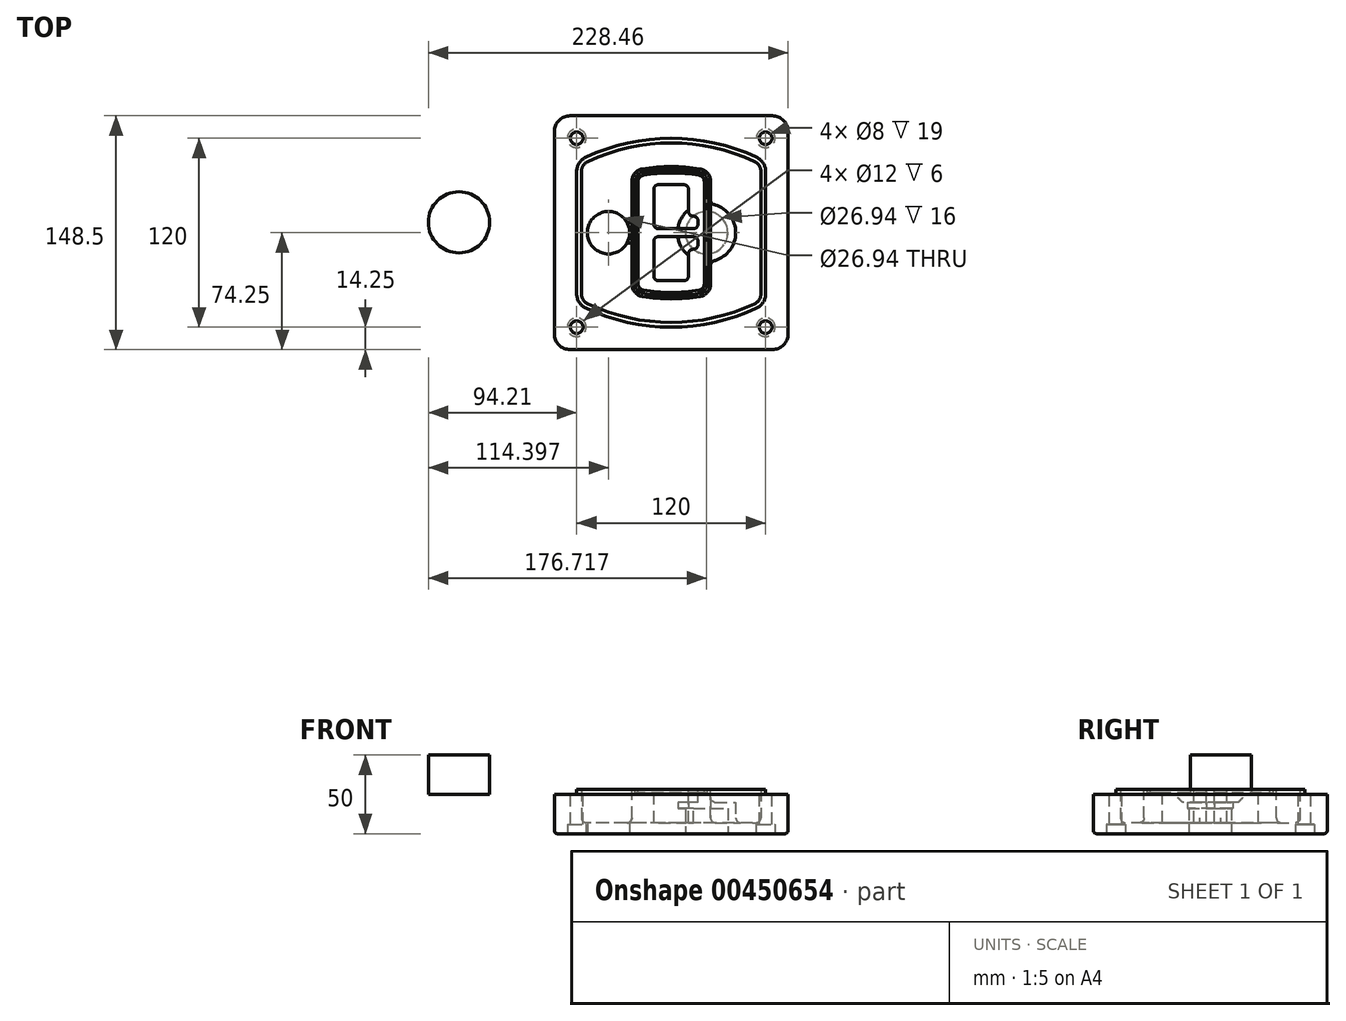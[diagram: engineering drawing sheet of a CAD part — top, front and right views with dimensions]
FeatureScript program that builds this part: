
annotation { "Feature Type Name" : "Feature", "Feature Type Description" : "" }
export const myFeature = defineFeature(function(context is Context, id is Id, definition is map)
    precondition{}
    {
        {
            var Q0;
            Q0=qCreatedBy(makeId("Top.planeOp"),FACE);
            var sketch = newSketch(context, id + "F0", { "sketchPlane" : qUnion([Q0])});
            skPoint(sketch, "E0.rect.middle", {"position": v(0, 0) * mm});
            skLineSegment(sketch, "E1.bottom", {"start": v(-64.25, -74.25) * mm, "end": v(64.25, -74.25) * mm});
            skLineSegment(sketch, "E1.top", {"start": v(-64.25, 74.25) * mm, "end": v(64.25, 74.25) * mm});
            skLineSegment(sketch, "E1.left", {"start": v(-74.25, -64.25) * mm, "end": v(-74.25, 64.25) * mm});
            skLineSegment(sketch, "E1.right", {"start": v(74.25, -64.25) * mm, "end": v(74.25, 64.25) * mm});
            skLineSegment(sketch, "E2", {"start": v(-74.25, 74.25) * mm, "end": v(74.25, -74.25) * mm, "construction": true});
            skLineSegment(sketch, "E3", {"start": v(74.25, 74.25) * mm, "end": v(-74.25, -74.25) * mm, "construction": true});
            skCircle(sketch, "E4", {"center": v(-60, 60) * mm, "radius": 4 * mm});
            skCircle(sketch, "E5", {"center": v(60, 60) * mm, "radius": 4 * mm});
            skCircle(sketch, "E6", {"center": v(60, -60) * mm, "radius": 4 * mm});
            skCircle(sketch, "E7", {"center": v(-60, -60) * mm, "radius": 4 * mm});
            skLineSegment(sketch, "E8", {"start": v(-60, 60) * mm, "end": v(60, 60) * mm, "construction": true});
            skLineSegment(sketch, "E9", {"start": v(60, 60) * mm, "end": v(60, -60) * mm, "construction": true});
            skLineSegment(sketch, "E10", {"start": v(60, -60) * mm, "end": v(-60, -60) * mm, "construction": true});
            skLineSegment(sketch, "E11", {"start": v(-60, -60) * mm, "end": v(-60, 60) * mm, "construction": true});
            skLineSegment(sketch, "E12", {"start": v(-60, 38.83) * mm, "end": v(-60, -38.83) * mm});
            skLineSegment(sketch, "E13", {"start": v(60, 38.83) * mm, "end": v(60, -38.83) * mm});
            skArc(sketch, "E14", {"start": v(54.26, 47.88) * mm, "mid": v(0, 60) * mm, "end": v(-54.26, 47.88) * mm});
            skArc(sketch, "E15", {"start": v(-54.26, -47.88) * mm, "mid": v(0, -60) * mm, "end": v(54.26, -47.88) * mm});
            skLineSegment(sketch, "E16", {"start": v(-60, 0) * mm, "end": v(60, 0) * mm, "construction": true});
            skPoint(sketch, "E17.visualSharp", {"position": v(-60, -45) * mm});
            skArc(sketch, "E17.filletArc", {"start": v(-60, -38.83) * mm, "mid": v(-58.44, -44.2) * mm, "end": v(-54.26, -47.88) * mm});
            skPoint(sketch, "E18.visualSharp", {"position": v(-60, 45) * mm});
            skArc(sketch, "E18.filletArc", {"start": v(-54.26, 47.88) * mm, "mid": v(-58.44, 44.2) * mm, "end": v(-60, 38.83) * mm});
            skPoint(sketch, "E19.visualSharp", {"position": v(60, 45) * mm});
            skArc(sketch, "E19.filletArc", {"start": v(60, 38.83) * mm, "mid": v(58.44, 44.2) * mm, "end": v(54.26, 47.88) * mm});
            skPoint(sketch, "E20.visualSharp", {"position": v(60, -45) * mm});
            skArc(sketch, "E20.filletArc", {"start": v(54.26, -47.88) * mm, "mid": v(58.44, -44.2) * mm, "end": v(60, -38.83) * mm});
            skPoint(sketch, "E21.visualSharp", {"position": v(-74.25, 74.25) * mm});
            skArc(sketch, "E21.filletArc", {"start": v(-64.25, 74.25) * mm, "mid": v(-71.32, 71.32) * mm, "end": v(-74.25, 64.25) * mm});
            skPoint(sketch, "E22.visualSharp", {"position": v(74.25, 74.25) * mm});
            skArc(sketch, "E22.filletArc", {"start": v(74.25, 64.25) * mm, "mid": v(71.32, 71.32) * mm, "end": v(64.25, 74.25) * mm});
            skPoint(sketch, "E23.visualSharp", {"position": v(74.25, -74.25) * mm});
            skArc(sketch, "E23.filletArc", {"start": v(64.25, -74.25) * mm, "mid": v(71.32, -71.32) * mm, "end": v(74.25, -64.25) * mm});
            skPoint(sketch, "E24.visualSharp", {"position": v(-74.25, -74.25) * mm});
            skArc(sketch, "E24.filletArc", {"start": v(-74.25, -64.25) * mm, "mid": v(-71.32, -71.32) * mm, "end": v(-64.25, -74.25) * mm});
            skArc(sketch, "E25.0", {"start": v(57, 38.83) * mm, "mid": v(55.9, 42.58) * mm, "end": v(52.98, 45.17) * mm});
            skLineSegment(sketch, "E25.1", {"start": v(57, 38.83) * mm, "end": v(57, -38.83) * mm});
            skArc(sketch, "E25.2", {"start": v(52.98, -45.17) * mm, "mid": v(55.9, -42.58) * mm, "end": v(57, -38.83) * mm});
            skArc(sketch, "E25.3", {"start": v(-52.98, -45.17) * mm, "mid": v(0, -57) * mm, "end": v(52.98, -45.17) * mm});
            skArc(sketch, "E25.4", {"start": v(-57, -38.83) * mm, "mid": v(-55.9, -42.58) * mm, "end": v(-52.98, -45.17) * mm});
            skArc(sketch, "E25.5", {"start": v(52.98, 45.17) * mm, "mid": v(0, 57) * mm, "end": v(-52.98, 45.17) * mm});
            skLineSegment(sketch, "E25.6", {"start": v(-57, 38.83) * mm, "end": v(-57, -38.83) * mm});
            skArc(sketch, "E25.7", {"start": v(-52.98, 45.17) * mm, "mid": v(-55.9, 42.58) * mm, "end": v(-57, 38.83) * mm});
            skArc(sketch, "E26.0", {"start": v(-55.96, 51.5) * mm, "mid": v(-61.82, 46.33) * mm, "end": v(-64, 38.83) * mm});
            skArc(sketch, "E26.1", {"start": v(55.96, 51.5) * mm, "mid": v(0, 64) * mm, "end": v(-55.96, 51.5) * mm});
            skArc(sketch, "E26.2", {"start": v(64, 38.83) * mm, "mid": v(61.82, 46.33) * mm, "end": v(55.96, 51.5) * mm});
            skLineSegment(sketch, "E26.3", {"start": v(64, 38.83) * mm, "end": v(64, -38.83) * mm});
            skArc(sketch, "E26.4", {"start": v(55.96, -51.5) * mm, "mid": v(61.82, -46.33) * mm, "end": v(64, -38.83) * mm});
            skLineSegment(sketch, "E26.5", {"start": v(-64, 38.83) * mm, "end": v(-64, -38.83) * mm});
            skArc(sketch, "E26.6", {"start": v(-55.96, -51.5) * mm, "mid": v(0, -64) * mm, "end": v(55.96, -51.5) * mm});
            skArc(sketch, "E26.7", {"start": v(-64, -38.83) * mm, "mid": v(-61.82, -46.33) * mm, "end": v(-55.96, -51.5) * mm});
            skSolve(sketch);
        }
        {
            var Q0;
            Q0=makeQuery(id+"F0.imprint","IMPRINT",FACE,{"disambiguationData":[TD([[makeQuery(id+"F0.imprint","IMPRINT",EDGE,{"derivedFrom":sQuery(id+"F0.wireOp",EDGE,"E1.bottom")}),1.0]])]});
            var Q1;
            Q1=makeQuery(id+"F0.imprint","IMPRINT",FACE,{"disambiguationData":[TD([[makeQuery(id+"F0.imprint","IMPRINT",EDGE,{"derivedFrom":sQuery(id+"F0.wireOp",EDGE,"E12")}),1.0]])]});
            var Q2;
            Q2=makeQuery(id+"F0.imprint","IMPRINT",FACE,{"disambiguationData":[TD([[makeQuery(id+"F0.imprint","IMPRINT",EDGE,{"derivedFrom":sQuery(id+"F0.wireOp",EDGE,"E25.0")}),1.0]])]});
            var Q3;
            Q3=makeQuery(id+"F0.imprint","IMPRINT",FACE,{"disambiguationData":[TD([[makeQuery(id+"F0.imprint","IMPRINT",EDGE,{"derivedFrom":sQuery(id+"F0.wireOp",EDGE,"E12")}),-1.0]])]});
            extrude(context, id + "F1", {"entities" : qUnion([Q0, Q1, Q2, Q3]), "oppositeDirection" : true, "depth" : 25 * mm});
        }
        {
            var Q0;
            Q0=makeQuery(id+"F0.imprint","IMPRINT",FACE,{"disambiguationData":[TD([[makeQuery(id+"F0.imprint","IMPRINT",EDGE,{"derivedFrom":sQuery(id+"F0.wireOp",EDGE,"E12")}),1.0]])]});
            extrude(context, id + "F2", {"entities" : qUnion([Q0]), "operationType" : NewBodyOperationType.ADD, "depth" : 3 * mm});
        }
        {
            var Q0;
            Q0=makeQuery(id+"F0.imprint","IMPRINT",FACE,{"disambiguationData":[TD([[makeQuery(id+"F0.imprint","IMPRINT",EDGE,{"derivedFrom":sQuery(id+"F0.wireOp",EDGE,"E25.0")}),1.0]])]});
            extrude(context, id + "F3", {"entities" : qUnion([Q0]), "operationType" : NewBodyOperationType.REMOVE, "oppositeDirection" : true, "depth" : 18 * mm});
        }
        {
            var Q0;
            Q0=makeQuery(id+"F2.opExtrude","CAP_FACE",FACE,{"disambiguationData":[OSD([sQuery(id+"F0.wireOp",EDGE,"E12"),sQuery(id+"F0.wireOp",EDGE,"E13"),sQuery(id+"F0.wireOp",EDGE,"E14"),sQuery(id+"F0.wireOp",EDGE,"E15"),sQuery(id+"F0.wireOp",EDGE,"E17.filletArc"),sQuery(id+"F0.wireOp",EDGE,"E18.filletArc"),sQuery(id+"F0.wireOp",EDGE,"E19.filletArc"),sQuery(id+"F0.wireOp",EDGE,"E20.filletArc"),sQuery(id+"F0.wireOp",EDGE,"E25.0"),sQuery(id+"F0.wireOp",EDGE,"E25.1"),sQuery(id+"F0.wireOp",EDGE,"E25.2"),sQuery(id+"F0.wireOp",EDGE,"E25.3"),sQuery(id+"F0.wireOp",EDGE,"E25.4"),sQuery(id+"F0.wireOp",EDGE,"E25.5"),sQuery(id+"F0.wireOp",EDGE,"E25.6"),sQuery(id+"F0.wireOp",EDGE,"E25.7")])],"isStart":false});
            var sketch = newSketch(context, id + "F4", { "sketchPlane" : qUnion([Q0])});
            skArc(sketch, "E27.0", {"start": v(-18.34, -40.45) * mm, "mid": v(0, -42) * mm, "end": v(18.34, -40.45) * mm});
            skArc(sketch, "E28.0", {"start": v(18.34, 40.45) * mm, "mid": v(0, 42) * mm, "end": v(-18.34, 40.45) * mm});
            skLineSegment(sketch, "E29", {"start": v(-25, 32.57) * mm, "end": v(-25, -32.57) * mm});
            skLineSegment(sketch, "E30", {"start": v(25, 32.57) * mm, "end": v(25, -32.57) * mm});
            skLineSegment(sketch, "E31", {"start": v(-25, 39.1) * mm, "end": v(25, 39.1) * mm, "construction": true});
            skLineSegment(sketch, "E32", {"start": v(-25, -39.1) * mm, "end": v(25, -39.1) * mm, "construction": true});
            skPoint(sketch, "E33.visualSharp", {"position": v(-25, 39.1) * mm});
            skArc(sketch, "E33.filletArc", {"start": v(-18.34, 40.45) * mm, "mid": v(-23.11, 37.73) * mm, "end": v(-25, 32.57) * mm});
            skPoint(sketch, "E34.visualSharp", {"position": v(25, 39.1) * mm});
            skArc(sketch, "E34.filletArc", {"start": v(25, 32.57) * mm, "mid": v(23.11, 37.73) * mm, "end": v(18.34, 40.45) * mm});
            skPoint(sketch, "E35.visualSharp", {"position": v(25, -39.1) * mm});
            skArc(sketch, "E35.filletArc", {"start": v(18.34, -40.45) * mm, "mid": v(23.11, -37.73) * mm, "end": v(25, -32.57) * mm});
            skPoint(sketch, "E36.visualSharp", {"position": v(-25, -39.1) * mm});
            skArc(sketch, "E36.filletArc", {"start": v(-25, -32.57) * mm, "mid": v(-23.11, -37.73) * mm, "end": v(-18.34, -40.45) * mm});
            skArc(sketch, "E37.0", {"start": v(52.98, 45.17) * mm, "mid": v(0, 57) * mm, "end": v(-52.98, 45.17) * mm});
            skArc(sketch, "E37.1", {"start": v(-52.98, 45.17) * mm, "mid": v(-55.9, 42.58) * mm, "end": v(-57, 38.83) * mm});
            skLineSegment(sketch, "E37.2", {"start": v(-57, 38.83) * mm, "end": v(-57, -38.83) * mm});
            skArc(sketch, "E37.3", {"start": v(-57, -38.83) * mm, "mid": v(-55.9, -42.58) * mm, "end": v(-52.98, -45.17) * mm});
            skArc(sketch, "E37.4", {"start": v(-52.98, -45.17) * mm, "mid": v(0, -57) * mm, "end": v(52.98, -45.17) * mm});
            skArc(sketch, "E37.5", {"start": v(52.98, -45.17) * mm, "mid": v(55.9, -42.58) * mm, "end": v(57, -38.83) * mm});
            skLineSegment(sketch, "E37.6", {"start": v(57, 38.83) * mm, "end": v(57, -38.83) * mm});
            skArc(sketch, "E37.7", {"start": v(57, 38.83) * mm, "mid": v(55.9, 42.58) * mm, "end": v(52.98, 45.17) * mm});
            skLineSegment(sketch, "E38.0", {"start": v(23, 32.57) * mm, "end": v(23, -32.57) * mm});
            skArc(sketch, "E38.1", {"start": v(18, -38.48) * mm, "mid": v(21.58, -36.44) * mm, "end": v(23, -32.57) * mm});
            skArc(sketch, "E38.2", {"start": v(-18, -38.48) * mm, "mid": v(0, -40) * mm, "end": v(18, -38.48) * mm});
            skArc(sketch, "E38.3", {"start": v(-23, -32.57) * mm, "mid": v(-21.58, -36.44) * mm, "end": v(-18, -38.48) * mm});
            skLineSegment(sketch, "E38.4", {"start": v(-23, 32.57) * mm, "end": v(-23, -32.57) * mm});
            skArc(sketch, "E38.5", {"start": v(23, 32.57) * mm, "mid": v(21.58, 36.44) * mm, "end": v(18, 38.48) * mm});
            skArc(sketch, "E38.6", {"start": v(-18, 38.48) * mm, "mid": v(-21.58, 36.44) * mm, "end": v(-23, 32.57) * mm});
            skArc(sketch, "E38.7", {"start": v(18, 38.48) * mm, "mid": v(0, 40) * mm, "end": v(-18, 38.48) * mm});
            skArc(sketch, "E39.0", {"start": v(21, 32.57) * mm, "mid": v(20.06, 35.15) * mm, "end": v(17.67, 36.5) * mm});
            skLineSegment(sketch, "E39.1", {"start": v(21, 32.57) * mm, "end": v(21, -32.57) * mm});
            skArc(sketch, "E39.2", {"start": v(17.67, -36.5) * mm, "mid": v(20.06, -35.15) * mm, "end": v(21, -32.57) * mm});
            skArc(sketch, "E39.3", {"start": v(-17.67, -36.5) * mm, "mid": v(0, -38) * mm, "end": v(17.67, -36.5) * mm});
            skArc(sketch, "E39.4", {"start": v(-21, -32.57) * mm, "mid": v(-20.06, -35.15) * mm, "end": v(-17.67, -36.5) * mm});
            skArc(sketch, "E39.5", {"start": v(17.67, 36.5) * mm, "mid": v(0, 38) * mm, "end": v(-17.67, 36.5) * mm});
            skLineSegment(sketch, "E39.6", {"start": v(-21, 32.57) * mm, "end": v(-21, -32.57) * mm});
            skArc(sketch, "E39.7", {"start": v(-17.67, 36.5) * mm, "mid": v(-20.06, 35.15) * mm, "end": v(-21, 32.57) * mm});
            skLineSegment(sketch, "E40", {"start": v(-25, 0) * mm, "end": v(25, 0) * mm, "construction": true});
            skLineSegment(sketch, "E41", {"start": v(-11, 5.5) * mm, "end": v(-11, 27.5) * mm});
            skLineSegment(sketch, "E42", {"start": v(-8, 30.5) * mm, "end": v(8, 30.5) * mm});
            skLineSegment(sketch, "E43", {"start": v(11, 27.5) * mm, "end": v(11, 13.5) * mm});
            skLineSegment(sketch, "E44", {"start": v(14, 10.5) * mm, "end": v(14, 10.5) * mm});
            skLineSegment(sketch, "E45", {"start": v(17, 7.5) * mm, "end": v(17, 5.5) * mm});
            skLineSegment(sketch, "E46", {"start": v(14, 2.5) * mm, "end": v(-8, 2.5) * mm});
            skPoint(sketch, "E47.visualSharp", {"position": v(-11, 30.5) * mm});
            skArc(sketch, "E47.filletArc", {"start": v(-8, 30.5) * mm, "mid": v(-10.12, 29.62) * mm, "end": v(-11, 27.5) * mm});
            skPoint(sketch, "E48.visualSharp", {"position": v(11, 30.5) * mm});
            skArc(sketch, "E48.filletArc", {"start": v(11, 27.5) * mm, "mid": v(10.12, 29.62) * mm, "end": v(8, 30.5) * mm});
            skPoint(sketch, "E49.visualSharp", {"position": v(11, 10.5) * mm});
            skArc(sketch, "E49.filletArc", {"start": v(11, 13.5) * mm, "mid": v(11.88, 11.38) * mm, "end": v(14, 10.5) * mm});
            skPoint(sketch, "E50.visualSharp", {"position": v(17, 10.5) * mm});
            skArc(sketch, "E50.filletArc", {"start": v(17, 7.5) * mm, "mid": v(16.12, 9.62) * mm, "end": v(14, 10.5) * mm});
            skPoint(sketch, "E51.visualSharp", {"position": v(17, 2.5) * mm});
            skArc(sketch, "E51.filletArc", {"start": v(14, 2.5) * mm, "mid": v(16.12, 3.38) * mm, "end": v(17, 5.5) * mm});
            skPoint(sketch, "E52.visualSharp", {"position": v(-11, 2.5) * mm});
            skArc(sketch, "E52.filletArc", {"start": v(-11, 5.5) * mm, "mid": v(-10.12, 3.38) * mm, "end": v(-8, 2.5) * mm});
            skLineSegment(sketch, "E53.0.MirrorCS", {"start": v(14, -2.5) * mm, "end": v(-8, -2.5) * mm});
            skArc(sketch, "E54.0.MirrorCS", {"start": v(-11, -5.5) * mm, "mid": v(-10.12, -3.38) * mm, "end": v(-8, -2.5) * mm});
            skLineSegment(sketch, "E55.0.MirrorCS", {"start": v(-11, -5.5) * mm, "end": v(-11, -27.5) * mm});
            skArc(sketch, "E56.0.MirrorCS", {"start": v(-8, -30.5) * mm, "mid": v(-10.12, -29.62) * mm, "end": v(-11, -27.5) * mm});
            skLineSegment(sketch, "E57.0.MirrorCS", {"start": v(-8, -30.5) * mm, "end": v(8, -30.5) * mm});
            skArc(sketch, "E58.0.MirrorCS", {"start": v(11, -27.5) * mm, "mid": v(10.12, -29.62) * mm, "end": v(8, -30.5) * mm});
            skLineSegment(sketch, "E59.0.MirrorCS", {"start": v(11, -27.5) * mm, "end": v(11, -13.5) * mm});
            skArc(sketch, "E60.0.MirrorCS", {"start": v(11, -13.5) * mm, "mid": v(11.88, -11.38) * mm, "end": v(14, -10.5) * mm});
            skArc(sketch, "E61.0.MirrorCS", {"start": v(17, -7.5) * mm, "mid": v(16.12, -9.62) * mm, "end": v(14, -10.5) * mm});
            skLineSegment(sketch, "E62.0.MirrorCS", {"start": v(17, -7.5) * mm, "end": v(17, -5.5) * mm});
            skArc(sketch, "E63.0.MirrorCS", {"start": v(14, -2.5) * mm, "mid": v(16.12, -3.38) * mm, "end": v(17, -5.5) * mm});
            skSolve(sketch);
        }
        {
            var Q0;
            Q0=makeQuery(id+"F4.imprint","IMPRINT",FACE,{"disambiguationData":[TD([[makeQuery(id+"F4.imprint","IMPRINT",EDGE,{"derivedFrom":sQuery(id+"F4.wireOp",EDGE,"E27.0")}),1.0]])]});
            var Q1;
            Q1=makeQuery(id+"F4.imprint","IMPRINT",FACE,{"disambiguationData":[TD([[makeQuery(id+"F4.imprint","IMPRINT",EDGE,{"derivedFrom":sQuery(id+"F4.wireOp",EDGE,"E38.0")}),-1.0]])]});
            var Q2;
            Q2=makeQuery(id+"F4.imprint","IMPRINT",FACE,{"disambiguationData":[TD([[makeQuery(id+"F4.imprint","IMPRINT",EDGE,{"derivedFrom":sQuery(id+"F4.wireOp",EDGE,"E39.0")}),1.0]])]});
            extrude(context, id + "F5", {"entities" : qUnion([Q0, Q1, Q2]), "operationType" : NewBodyOperationType.ADD, "endBound" : BoundingType.UP_TO_NEXT, "oppositeDirection" : true, "depth" : 25 * mm});
        }
        {
            var Q0;
            Q0=makeQuery(id+"F4.imprint","IMPRINT",FACE,{"disambiguationData":[TD([[makeQuery(id+"F4.imprint","IMPRINT",EDGE,{"derivedFrom":sQuery(id+"F4.wireOp",EDGE,"E38.0")}),-1.0]])]});
            extrude(context, id + "F6", {"entities" : qUnion([Q0]), "operationType" : NewBodyOperationType.REMOVE, "oppositeDirection" : true, "depth" : 2 * mm});
        }
        {
            var Q0;
            Q0=makeQuery(id+"F1.opExtrude","CAP_FACE",FACE,{"disambiguationData":[OSD([sQuery(id+"F0.wireOp",EDGE,"E1.bottom"),sQuery(id+"F0.wireOp",EDGE,"E1.top"),sQuery(id+"F0.wireOp",EDGE,"E1.left"),sQuery(id+"F0.wireOp",EDGE,"E1.right"),sQuery(id+"F0.wireOp",EDGE,"E4"),sQuery(id+"F0.wireOp",EDGE,"E5"),sQuery(id+"F0.wireOp",EDGE,"E6"),sQuery(id+"F0.wireOp",EDGE,"E7"),sQuery(id+"F0.wireOp",EDGE,"E21.filletArc"),sQuery(id+"F0.wireOp",EDGE,"E22.filletArc"),sQuery(id+"F0.wireOp",EDGE,"E23.filletArc"),sQuery(id+"F0.wireOp",EDGE,"E24.filletArc")])],"isStart":false});
            var sketch = newSketch(context, id + "F7", { "sketchPlane" : qUnion([Q0])});
            skCircle(sketch, "E64", {"center": v(22.5, 0) * mm, "radius": 13.47 * mm});
            skCircle(sketch, "E65", {"center": v(-39.81, 0) * mm, "radius": 13.47 * mm});
            skLineSegment(sketch, "E66", {"start": v(74.25, 0) * mm, "end": v(-74.25, 0) * mm});
            skCircle(sketch, "E67", {"center": v(22.5, 0) * mm, "radius": 18.47 * mm});
            skCircle(sketch, "E68", {"center": v(60, -60) * mm, "radius": 6 * mm});
            skCircle(sketch, "E69", {"center": v(-60, -60) * mm, "radius": 6 * mm});
            skCircle(sketch, "E70", {"center": v(-60, 60) * mm, "radius": 6 * mm});
            skCircle(sketch, "E71", {"center": v(60, 60) * mm, "radius": 6 * mm});
            skSolve(sketch);
        }
        {
            var Q0;
            {var subQ1=sQuery(id+"F7.wireOp",EDGE,"E66");var subQ4=sQuery(id+"F7.wireOp",EDGE,"E64");var subQ6=makeQuery(id+"F7.imprint","INTERSECT",VERTEX,{"disambiguationData":[OD(0.0)],"derivedFrom":[subQ4,subQ1]});Q0=makeQuery(id+"F7.imprint","IMPRINT",FACE,{"disambiguationData":[TD([[makeQuery(id+"F7.imprint","IMPRINT",EDGE,{"disambiguationData":[TD([[subQ6,-1.0]])],"derivedFrom":subQ4}),-1.0]])]});}
            var Q1;
            {var subQ0=sQuery(id+"F7.wireOp",EDGE,"E66");var subQ1=sQuery(id+"F7.wireOp",EDGE,"E64");var subQ3=makeQuery(id+"F7.imprint","INTERSECT",VERTEX,{"disambiguationData":[OD(0.0)],"derivedFrom":[subQ1,subQ0]});Q1=makeQuery(id+"F7.imprint","IMPRINT",FACE,{"disambiguationData":[TD([[makeQuery(id+"F7.imprint","IMPRINT",EDGE,{"disambiguationData":[TD([[subQ3,-1.0]])],"derivedFrom":subQ1}),1.0]])]});}
            var Q2;
            {var subQ0=sQuery(id+"F7.wireOp",EDGE,"E66");var subQ1=sQuery(id+"F7.wireOp",EDGE,"E64");var subQ3=makeQuery(id+"F7.imprint","INTERSECT",VERTEX,{"disambiguationData":[OD(0.0)],"derivedFrom":[subQ1,subQ0]});Q2=makeQuery(id+"F7.imprint","IMPRINT",FACE,{"disambiguationData":[TD([[makeQuery(id+"F7.imprint","IMPRINT",EDGE,{"disambiguationData":[TD([[subQ3,1.0]])],"derivedFrom":subQ1}),1.0]])]});}
            var Q3;
            {var subQ1=sQuery(id+"F7.wireOp",EDGE,"E66");var subQ4=sQuery(id+"F7.wireOp",EDGE,"E64");var subQ6=makeQuery(id+"F7.imprint","INTERSECT",VERTEX,{"disambiguationData":[OD(0.0)],"derivedFrom":[subQ4,subQ1]});Q3=makeQuery(id+"F7.imprint","IMPRINT",FACE,{"disambiguationData":[TD([[makeQuery(id+"F7.imprint","IMPRINT",EDGE,{"disambiguationData":[TD([[subQ6,1.0]])],"derivedFrom":subQ4}),-1.0]])]});}
            extrude(context, id + "F8", {"entities" : qUnion([Q0, Q1, Q2, Q3]), "operationType" : NewBodyOperationType.ADD, "oppositeDirection" : true, "depth" : 20 * mm});
        }
        {
            var Q0;
            {var subQ0=sQuery(id+"F7.wireOp",EDGE,"E66");var subQ1=sQuery(id+"F7.wireOp",EDGE,"E64");var subQ3=makeQuery(id+"F7.imprint","INTERSECT",VERTEX,{"disambiguationData":[OD(0.0)],"derivedFrom":[subQ1,subQ0]});Q0=makeQuery(id+"F7.imprint","IMPRINT",FACE,{"disambiguationData":[TD([[makeQuery(id+"F7.imprint","IMPRINT",EDGE,{"disambiguationData":[TD([[subQ3,-1.0]])],"derivedFrom":subQ1}),1.0]])]});}
            var Q1;
            {var subQ0=sQuery(id+"F7.wireOp",EDGE,"E66");var subQ1=sQuery(id+"F7.wireOp",EDGE,"E64");var subQ3=makeQuery(id+"F7.imprint","INTERSECT",VERTEX,{"disambiguationData":[OD(0.0)],"derivedFrom":[subQ1,subQ0]});Q1=makeQuery(id+"F7.imprint","IMPRINT",FACE,{"disambiguationData":[TD([[makeQuery(id+"F7.imprint","IMPRINT",EDGE,{"disambiguationData":[TD([[subQ3,1.0]])],"derivedFrom":subQ1}),1.0]])]});}
            extrude(context, id + "F9", {"entities" : qUnion([Q0, Q1]), "operationType" : NewBodyOperationType.REMOVE, "oppositeDirection" : true, "depth" : 16 * mm});
        }
        {
            var Q0;
            {var subQ0=sQuery(id+"F7.wireOp",EDGE,"E66");var subQ1=sQuery(id+"F7.wireOp",EDGE,"E65");var subQ3=makeQuery(id+"F7.imprint","INTERSECT",VERTEX,{"disambiguationData":[OD(0.0)],"derivedFrom":[subQ1,subQ0]});Q0=makeQuery(id+"F7.imprint","IMPRINT",FACE,{"disambiguationData":[TD([[makeQuery(id+"F7.imprint","IMPRINT",EDGE,{"disambiguationData":[TD([[subQ3,-1.0]])],"derivedFrom":subQ1}),1.0]])]});}
            var Q1;
            {var subQ0=sQuery(id+"F7.wireOp",EDGE,"E66");var subQ1=sQuery(id+"F7.wireOp",EDGE,"E65");var subQ3=makeQuery(id+"F7.imprint","INTERSECT",VERTEX,{"disambiguationData":[OD(0.0)],"derivedFrom":[subQ1,subQ0]});Q1=makeQuery(id+"F7.imprint","IMPRINT",FACE,{"disambiguationData":[TD([[makeQuery(id+"F7.imprint","IMPRINT",EDGE,{"disambiguationData":[TD([[subQ3,1.0]])],"derivedFrom":subQ1}),1.0]])]});}
            extrude(context, id + "F10", {"entities" : qUnion([Q0, Q1]), "operationType" : NewBodyOperationType.REMOVE, "oppositeDirection" : true, "depth" : 25 * mm});
        }
        {
            var Q0;
            Q0=makeQuery(id+"F7.imprint","IMPRINT",FACE,{"disambiguationData":[TD([[makeQuery(id+"F7.imprint","IMPRINT",EDGE,{"derivedFrom":sQuery(id+"F7.wireOp",EDGE,"E68")}),1.0]])]});
            var Q1;
            Q1=makeQuery(id+"F7.imprint","IMPRINT",FACE,{"disambiguationData":[TD([[makeQuery(id+"F7.imprint","IMPRINT",EDGE,{"derivedFrom":makeQuery(id+"F1.opExtrude","CAP_EDGE",EDGE,{"disambiguationData":[OSD([sQuery(id+"F0.wireOp",EDGE,"E5")])],"isStart":false})}),-1.0]])]});
            var Q2;
            Q2=makeQuery(id+"F7.imprint","IMPRINT",FACE,{"disambiguationData":[TD([[makeQuery(id+"F7.imprint","IMPRINT",EDGE,{"derivedFrom":sQuery(id+"F7.wireOp",EDGE,"E69")}),1.0]])]});
            var Q3;
            Q3=makeQuery(id+"F7.imprint","IMPRINT",FACE,{"disambiguationData":[TD([[makeQuery(id+"F7.imprint","IMPRINT",EDGE,{"derivedFrom":makeQuery(id+"F1.opExtrude","CAP_EDGE",EDGE,{"disambiguationData":[OSD([sQuery(id+"F0.wireOp",EDGE,"E4")])],"isStart":false})}),-1.0]])]});
            var Q4;
            Q4=makeQuery(id+"F7.imprint","IMPRINT",FACE,{"disambiguationData":[TD([[makeQuery(id+"F7.imprint","IMPRINT",EDGE,{"derivedFrom":sQuery(id+"F7.wireOp",EDGE,"E70")}),1.0]])]});
            var Q5;
            Q5=makeQuery(id+"F7.imprint","IMPRINT",FACE,{"disambiguationData":[TD([[makeQuery(id+"F7.imprint","IMPRINT",EDGE,{"derivedFrom":makeQuery(id+"F1.opExtrude","CAP_EDGE",EDGE,{"disambiguationData":[OSD([sQuery(id+"F0.wireOp",EDGE,"E7")])],"isStart":false})}),-1.0]])]});
            var Q6;
            Q6=makeQuery(id+"F7.imprint","IMPRINT",FACE,{"disambiguationData":[TD([[makeQuery(id+"F7.imprint","IMPRINT",EDGE,{"derivedFrom":sQuery(id+"F7.wireOp",EDGE,"E71")}),1.0]])]});
            var Q7;
            Q7=makeQuery(id+"F7.imprint","IMPRINT",FACE,{"disambiguationData":[TD([[makeQuery(id+"F7.imprint","IMPRINT",EDGE,{"derivedFrom":makeQuery(id+"F1.opExtrude","CAP_EDGE",EDGE,{"disambiguationData":[OSD([sQuery(id+"F0.wireOp",EDGE,"E6")])],"isStart":false})}),-1.0]])]});
            extrude(context, id + "F11", {"entities" : qUnion([Q0, Q1, Q2, Q3, Q4, Q5, Q6, Q7]), "operationType" : NewBodyOperationType.REMOVE, "oppositeDirection" : true, "depth" : 6 * mm});
        }
        {
            var Q0;
            Q0=makeQuery(id+"F9.boolean.opBoolean","COPY",FACE,{"derivedFrom":makeQuery(id+"F9.opExtrude","CAP_FACE",FACE,{"disambiguationData":[OSD([sQuery(id+"F7.wireOp",EDGE,"E64")])],"isStart":false})});
            var sketch = newSketch(context, id + "F12", { "sketchPlane" : qUnion([Q0])});
            skArc(sketch, "E72.0", {"start": v(11, 14.45) * mm, "mid": v(6.45, 9.13) * mm, "end": v(4.2, 2.5) * mm});
            skArc(sketch, "E72.1", {"start": v(4.2, -2.5) * mm, "mid": v(6.45, -9.13) * mm, "end": v(11, -14.45) * mm});
            skLineSegment(sketch, "E73", {"start": v(4.2, -2.5) * mm, "end": v(14, -2.5) * mm});
            skLineSegment(sketch, "E74.0", {"start": v(14, 2.5) * mm, "end": v(4.2, 2.5) * mm});
            skArc(sketch, "E74.1", {"start": v(14, 2.5) * mm, "mid": v(16.12, 3.38) * mm, "end": v(17, 5.5) * mm});
            skLineSegment(sketch, "E74.2", {"start": v(17, 7.5) * mm, "end": v(17, 5.5) * mm});
            skArc(sketch, "E74.3", {"start": v(17, 7.5) * mm, "mid": v(16.12, 9.62) * mm, "end": v(14, 10.5) * mm});
            skArc(sketch, "E74.4", {"start": v(11, 13.5) * mm, "mid": v(11.88, 11.38) * mm, "end": v(14, 10.5) * mm});
            skLineSegment(sketch, "E74.5", {"start": v(11, 14.45) * mm, "end": v(11, 13.5) * mm});
            skLineSegment(sketch, "E74.7", {"start": v(14, -2.5) * mm, "end": v(4.2, -2.5) * mm});
            skArc(sketch, "E74.8", {"start": v(14, -2.5) * mm, "mid": v(16.12, -3.38) * mm, "end": v(17, -5.5) * mm});
            skLineSegment(sketch, "E74.9", {"start": v(17, -7.5) * mm, "end": v(17, -5.5) * mm});
            skArc(sketch, "E74.10", {"start": v(17, -7.5) * mm, "mid": v(16.12, -9.62) * mm, "end": v(14, -10.5) * mm});
            skArc(sketch, "E74.11", {"start": v(11, -13.5) * mm, "mid": v(11.88, -11.38) * mm, "end": v(14, -10.5) * mm});
            skLineSegment(sketch, "E74.12", {"start": v(11, -14.45) * mm, "end": v(11, -13.5) * mm});
            skPoint(sketch, "E75.orphan", {"position": v(11, -27.5) * mm});
            skPoint(sketch, "E76.orphan", {"position": v(-8, -2.5) * mm});
            skPoint(sketch, "E77.orphan", {"position": v(-8, 2.5) * mm});
            skPoint(sketch, "E78.orphan", {"position": v(11, 27.5) * mm});
            skSolve(sketch);
        }
        {
            var Q0;
            {var subQ7=sQuery(id+"F12.wireOp",EDGE,"E72.0");var subQ14=sQuery(id+"F12.wireOp",EDGE,"E72.1");var subQ16=sQuery(id+"F12.wireOp",EDGE,"E74.1");var subQ18=sQuery(id+"F12.wireOp",EDGE,"E74.8");Q0=qUnion([makeQuery(id+"F12.imprint","IMPRINT",FACE,{"disambiguationData":[TD([[makeQuery(id+"F12.imprint","IMPRINT",EDGE,{"derivedFrom":subQ7}),1.0]])]}),makeQuery(id+"F12.imprint","IMPRINT",FACE,{"disambiguationData":[TD([[makeQuery(id+"F12.imprint","IMPRINT",EDGE,{"derivedFrom":subQ14}),1.0]])]}),makeQuery(id+"F12.imprint","IMPRINT",FACE,{"disambiguationData":[TD([[makeQuery(id+"F12.imprint","IMPRINT",EDGE,{"derivedFrom":subQ16}),1.0]])]}),makeQuery(id+"F12.imprint","IMPRINT",FACE,{"disambiguationData":[TD([[makeQuery(id+"F12.imprint","IMPRINT",EDGE,{"derivedFrom":subQ18}),-1.0]])]})]);}
            var Q1;
            Q1=makeQuery(id+"F5.boolean.opBoolean","SPLIT",FACE,{"disambiguationData":[TD([makeQuery(id+"F5.opExtrude","SWEPT_FACE",FACE,{"disambiguationData":[OSD([sQuery(id+"F4.wireOp",EDGE,"E41")])]})])],"derivedFrom":makeQuery(id+"F3.boolean.opBoolean","COPY",FACE,{"derivedFrom":makeQuery(id+"F3.opExtrude","CAP_FACE",FACE,{"disambiguationData":[OSD([sQuery(id+"F0.wireOp",EDGE,"E25.0"),sQuery(id+"F0.wireOp",EDGE,"E25.1"),sQuery(id+"F0.wireOp",EDGE,"E25.2"),sQuery(id+"F0.wireOp",EDGE,"E25.3"),sQuery(id+"F0.wireOp",EDGE,"E25.4"),sQuery(id+"F0.wireOp",EDGE,"E25.5"),sQuery(id+"F0.wireOp",EDGE,"E25.6"),sQuery(id+"F0.wireOp",EDGE,"E25.7")])],"isStart":false})})});
            extrude(context, id + "F13", {"entities" : qUnion([Q0]), "operationType" : NewBodyOperationType.REMOVE, "endBound" : BoundingType.UP_TO_SURFACE, "endBoundEntityFace" : qUnion([Q1]), "depth" : 25 * mm});
        }
        {
            var Q0;
            Q0=makeQuery(id+"F3.boolean.opBoolean","COPY",EDGE,{"derivedFrom":makeQuery(id+"F3.opExtrude","CAP_EDGE",EDGE,{"disambiguationData":[OSD([sQuery(id+"F0.wireOp",EDGE,"E25.6")])],"isStart":false})});
            var Q1;
            Q1=makeQuery(id+"F8.boolean.opBoolean","INTERSECT",EDGE,{"derivedFrom":[makeQuery(id+"F5.opExtrude","SWEPT_FACE",FACE,{"disambiguationData":[OSD([sQuery(id+"F4.wireOp",EDGE,"E30")])]}),makeQuery(id+"F8.opExtrude","CAP_FACE",FACE,{"disambiguationData":[OSD([sQuery(id+"F7.wireOp",EDGE,"E67")])],"isStart":false})]});
            var Q2;
            Q2=makeQuery(id+"F8.boolean.opBoolean","INTERSECT",EDGE,{"disambiguationData":[OD(1.0)],"derivedFrom":[makeQuery(id+"F5.opExtrude","SWEPT_FACE",FACE,{"disambiguationData":[OSD([sQuery(id+"F4.wireOp",EDGE,"E30")])]}),makeQuery(id+"F8.opExtrude","SWEPT_FACE",FACE,{"disambiguationData":[OSD([sQuery(id+"F7.wireOp",EDGE,"E67")])]})]});
            var Q3;
            {var subQ0=sQuery(id+"F4.wireOp",EDGE,"E30");Q3=makeQuery(id+"F8.boolean.opBoolean","SPLIT",EDGE,{"disambiguationData":[TD([makeQuery(id+"F5.opExtrude","SWEPT_FACE",FACE,{"disambiguationData":[OSD([sQuery(id+"F4.wireOp",EDGE,"E35.filletArc")])]})])],"derivedFrom":makeQuery(id+"F5.opExtrude","CAP_EDGE",EDGE,{"disambiguationData":[OSD([subQ0])],"isStart":false})});}
            var Q4;
            {var subQ0=sQuery(id+"F0.wireOp",EDGE,"E25.7");var subQ1=sQuery(id+"F0.wireOp",EDGE,"E25.1");var subQ2=sQuery(id+"F0.wireOp",EDGE,"E25.6");var subQ3=sQuery(id+"F0.wireOp",EDGE,"E25.5");var subQ4=sQuery(id+"F0.wireOp",EDGE,"E25.4");var subQ5=sQuery(id+"F0.wireOp",EDGE,"E25.0");var subQ6=sQuery(id+"F0.wireOp",EDGE,"E25.2");var subQ7=sQuery(id+"F0.wireOp",EDGE,"E25.3");Q4=makeQuery(id+"F8.boolean.opBoolean","INTERSECT",EDGE,{"derivedFrom":[makeQuery(id+"F5.boolean.opBoolean","SPLIT",FACE,{"disambiguationData":[TD([makeQuery(id+"F2.opExtrude","SWEPT_FACE",FACE,{"disambiguationData":[OSD([subQ5])]})])],"derivedFrom":makeQuery(id+"F3.boolean.opBoolean","COPY",FACE,{"derivedFrom":makeQuery(id+"F3.opExtrude","CAP_FACE",FACE,{"disambiguationData":[OSD([subQ5,subQ1,subQ6,subQ7,subQ4,subQ3,subQ2,subQ0])],"isStart":false})})}),makeQuery(id+"F8.opExtrude","SWEPT_FACE",FACE,{"disambiguationData":[OSD([sQuery(id+"F7.wireOp",EDGE,"E67")])]})]});}
            var Q5;
            Q5=makeQuery(id+"F8.boolean.opBoolean","INTERSECT",EDGE,{"disambiguationData":[OD(0.0)],"derivedFrom":[makeQuery(id+"F5.opExtrude","SWEPT_FACE",FACE,{"disambiguationData":[OSD([sQuery(id+"F4.wireOp",EDGE,"E30")])]}),makeQuery(id+"F8.opExtrude","SWEPT_FACE",FACE,{"disambiguationData":[OSD([sQuery(id+"F7.wireOp",EDGE,"E67")])]})]});
            fillet(context, id + "F14", {"entities" : qUnion([Q0, Q1, Q2, Q3, Q4, Q5]), "radius" : 3 * mm, "tangentPropagation" : true, "allowEdgeOverflow" : false});
        }
        {
            var Q0;
            Q0=makeQuery(id+"F1.opExtrude","CAP_EDGE",EDGE,{"disambiguationData":[OSD([sQuery(id+"F0.wireOp",EDGE,"E1.bottom")])],"isStart":false});
            fillet(context, id + "F15", {"entities" : qUnion([Q0]), "radius" : 2 * mm, "tangentPropagation" : true, "allowEdgeOverflow" : false});
        }
        {
            var Q0;
            {var subQ0=sQuery(id+"F0.wireOp",EDGE,"E21.filletArc");var subQ1=sQuery(id+"F0.wireOp",EDGE,"E7");var subQ2=sQuery(id+"F0.wireOp",EDGE,"E6");var subQ3=sQuery(id+"F0.wireOp",EDGE,"E5");var subQ4=sQuery(id+"F0.wireOp",EDGE,"E4");var subQ5=sQuery(id+"F0.wireOp",EDGE,"E22.filletArc");var subQ6=sQuery(id+"F0.wireOp",EDGE,"E1.bottom");var subQ7=sQuery(id+"F0.wireOp",EDGE,"E1.right");var subQ8=sQuery(id+"F0.wireOp",EDGE,"E1.top");var subQ9=sQuery(id+"F0.wireOp",EDGE,"E1.left");var subQ10=sQuery(id+"F0.wireOp",EDGE,"E23.filletArc");var subQ11=sQuery(id+"F0.wireOp",EDGE,"E24.filletArc");Q0=makeQuery(id+"F2.boolean.opBoolean","SPLIT",FACE,{"disambiguationData":[TD([makeQuery(id+"F1.opExtrude","SWEPT_FACE",FACE,{"disambiguationData":[OSD([subQ6])]})])],"derivedFrom":makeQuery(id+"F1.opExtrude","CAP_FACE",FACE,{"disambiguationData":[OSD([subQ6,subQ8,subQ9,subQ7,subQ4,subQ3,subQ2,subQ1,subQ0,subQ5,subQ10,subQ11])],"isStart":true})});}
            var sketch = newSketch(context, id + "F16", { "sketchPlane" : qUnion([Q0])});
            skCircle(sketch, "E79", {"center": v(-134.8, 6.62) * mm, "radius": 19.41 * mm});
            skSolve(sketch);
        }
        {
            var Q0;
            Q0 = qSketchRegion(id + "F16", true);
            extrude(context, id + "F17", {"entities" : qUnion([Q0]), "depth" : 25 * mm});
        }
    });
